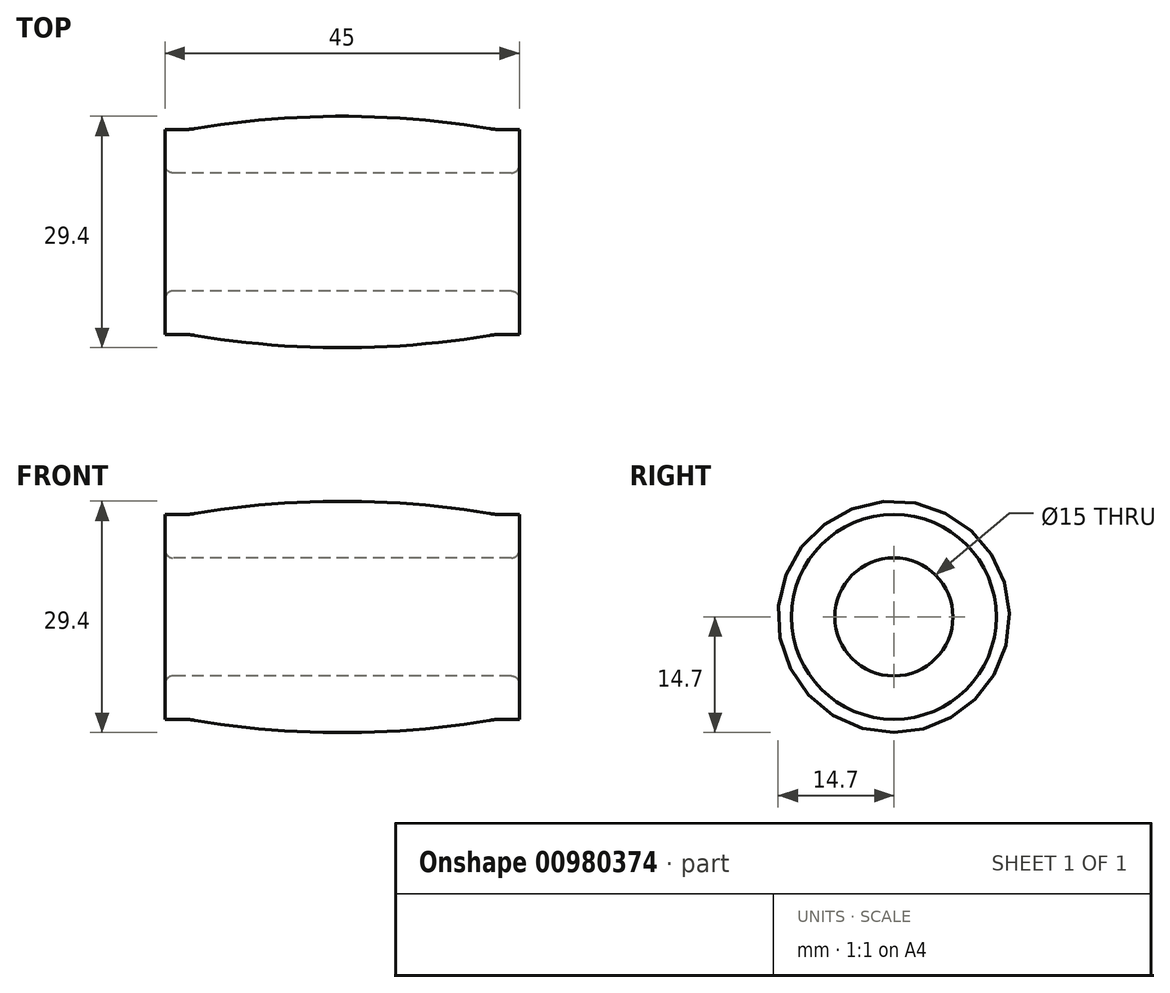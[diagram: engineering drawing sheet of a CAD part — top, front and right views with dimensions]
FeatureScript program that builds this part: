
annotation { "Feature Type Name" : "Feature", "Feature Type Description" : "" }
export const myFeature = defineFeature(function(context is Context, id is Id, definition is map)
    precondition{}
    {
        {
            var Q0;
            Q0=qCreatedBy(makeId("Front.planeOp"),FACE);
            var sketch = newSketch(context, id + "F0", { "sketchPlane" : qUnion([Q0])});
            skLineSegment(sketch, "E0", {"start": v(0, 13) * mm, "end": v(3, 13) * mm});
            skLineSegment(sketch, "E1", {"start": v(45, 13) * mm, "end": v(45, 8.5) * mm});
            skLineSegment(sketch, "E2", {"start": v(44, 7.5) * mm, "end": v(1, 7.5) * mm});
            skLineSegment(sketch, "E3", {"start": v(0, 8.5) * mm, "end": v(0, 13) * mm});
            skPoint(sketch, "E4.visualSharp", {"position": v(0, 7.5) * mm});
            skArc(sketch, "E4.filletArc", {"start": v(0, 8.5) * mm, "mid": v(0.3, 7.8) * mm, "end": v(1, 7.5) * mm});
            skPoint(sketch, "E5.visualSharp", {"position": v(45, 7.5) * mm});
            skArc(sketch, "E5.filletArc", {"start": v(44, 7.5) * mm, "mid": v(44.7, 7.8) * mm, "end": v(45, 8.5) * mm});
            skArc(sketch, "E6", {"start": v(42, 13) * mm, "mid": v(22.5, 14.7) * mm, "end": v(3, 13) * mm});
            skLineSegment(sketch, "E7.trimOffspring", {"start": v(42, 13) * mm, "end": v(45, 13) * mm});
            skLineSegment(sketch, "E8", {"start": v(0, 0) * mm, "end": v(18.88, 0) * mm});
            skSolve(sketch);
        }
        {
            var Q0;
            Q0 = qSketchRegion(id + "F0", true);
            var Q1;
            Q1=sQuery(id+"F0.wireOp",EDGE,"E8");
            revolve(context, id + "F1", {"surfaceOperationType" : NewSurfaceOperationType.NEW, "entities" : qUnion([Q0]), "axis" : qUnion([Q1]), "revolveType" : RevolveType.FULL});
        }
        {
            var Q0;
            Q0=makeQuery(id+"F1.opRevolve","SWEPT_EDGE",EDGE,{"disambiguationData":[OSD([sQuery(id+"F0.wireOp",EDGE,"E0"),sQuery(id+"F0.wireOp",EDGE,"E6")])]});
            var Q1;
            Q1=makeQuery(id+"F1.opRevolve","SWEPT_EDGE",EDGE,{"disambiguationData":[OSD([sQuery(id+"F0.wireOp",EDGE,"E6"),sQuery(id+"F0.wireOp",EDGE,"E7.trimOffspring")])]});
            fillet(context, id + "F2", {"entities" : qUnion([Q0, Q1]), "radius" : 10 * mm, "tangentPropagation" : true, "allowEdgeOverflow" : false});
        }
    });
